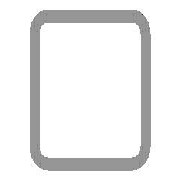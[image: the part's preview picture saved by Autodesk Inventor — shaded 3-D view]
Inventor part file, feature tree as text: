
AUTODESK INVENTOR PART (.ipt)
format: ipt  version: 2024 (Build 280153000, 153)  size: 152,576 bytes
history: native  units: mm (DEFAULTED — no unit token found)
features: other x4, plane x2, split x1, sketch x1
ambient origin geometry x8: Origin, YZ Plane, XZ Plane, XY Plane, X Axis, Y Axis, Z Axis, Center Point
bodies: Solid1 (feature_tree), Body (feature_tree)
feature tree (8):
  parser-record x1  (decoder bookkeeping rows leaked as tree rows — omitted from the tree; the rows remain in map.json)
  other  "Driven Length"
  other  "Start Plane"
  other  "End Plane"
  plane  "Work Plane4"
  split  "Split1"
  sketch  "Sketch3"  dims[d3=3173.282863mm d4=0.0mm d7=7.5mm d10=100.0mm d11=100.0mm d12=5.0mm d13=-0.0mm d14=3173.282863mm d15=50.0mm d16=50.0mm d17=90.0deg d18=3173.282863mm d19=5.0mm d20=5.0mm]
  plane  "Work Plane3"
